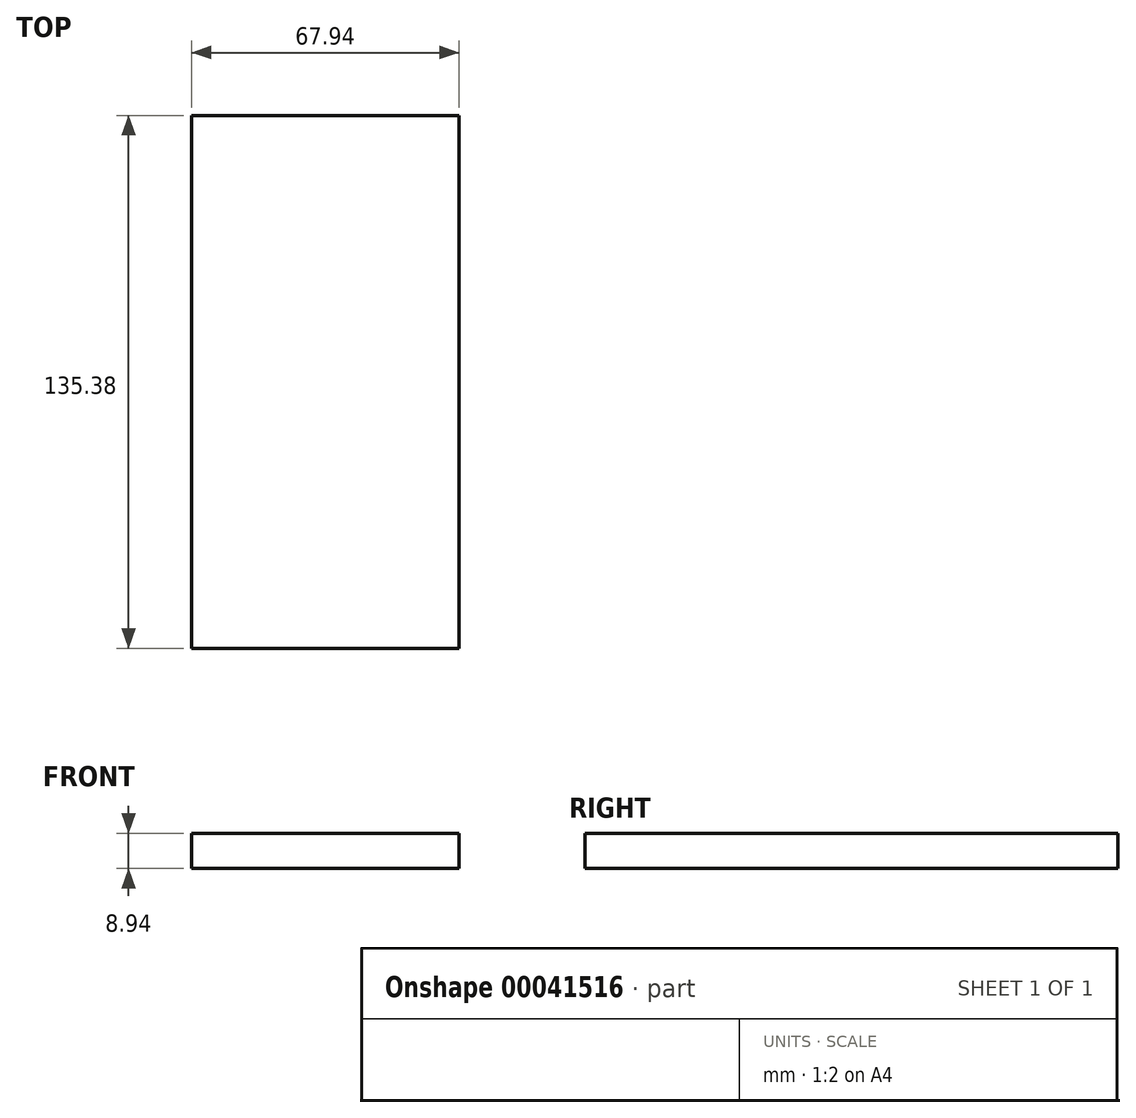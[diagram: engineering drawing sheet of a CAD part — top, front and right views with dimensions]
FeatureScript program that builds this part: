
annotation { "Feature Type Name" : "Feature", "Feature Type Description" : "" }
export const myFeature = defineFeature(function(context is Context, id is Id, definition is map)
    precondition{}
    {
        {
            var Q0;
            Q0=qCreatedBy(makeId("Top.planeOp"),FACE);
            var sketch = newSketch(context, id + "F0", { "sketchPlane" : qUnion([Q0])});
            skLineSegment(sketch, "E0.rect.bottom", {"start": v(33.97, -67.7) * mm, "end": v(-33.97, -67.7) * mm});
            skLineSegment(sketch, "E0.rect.top", {"start": v(33.97, 67.7) * mm, "end": v(-33.97, 67.7) * mm});
            skLineSegment(sketch, "E0.rect.left", {"start": v(33.97, -67.7) * mm, "end": v(33.97, 67.7) * mm});
            skLineSegment(sketch, "E0.rect.right", {"start": v(-33.97, -67.7) * mm, "end": v(-33.97, 67.7) * mm});
            skPoint(sketch, "E0.rect.middle", {"position": v(0, 0) * mm});
            skSolve(sketch);
        }
        {
            var Q0;
            Q0=makeQuery(id+"F0.imprint","IMPRINT",FACE,{"disambiguationData":[TD([[makeQuery(id+"F0.imprint","IMPRINT",EDGE,{"derivedFrom":sQuery(id+"F0.wireOp",EDGE,"E0.rect.bottom")}),-1.0]])]});
            extrude(context, id + "F1", {"entities" : qUnion([Q0]), "oppositeDirection" : true, "depth" : 8.94 * mm});
        }
    });
